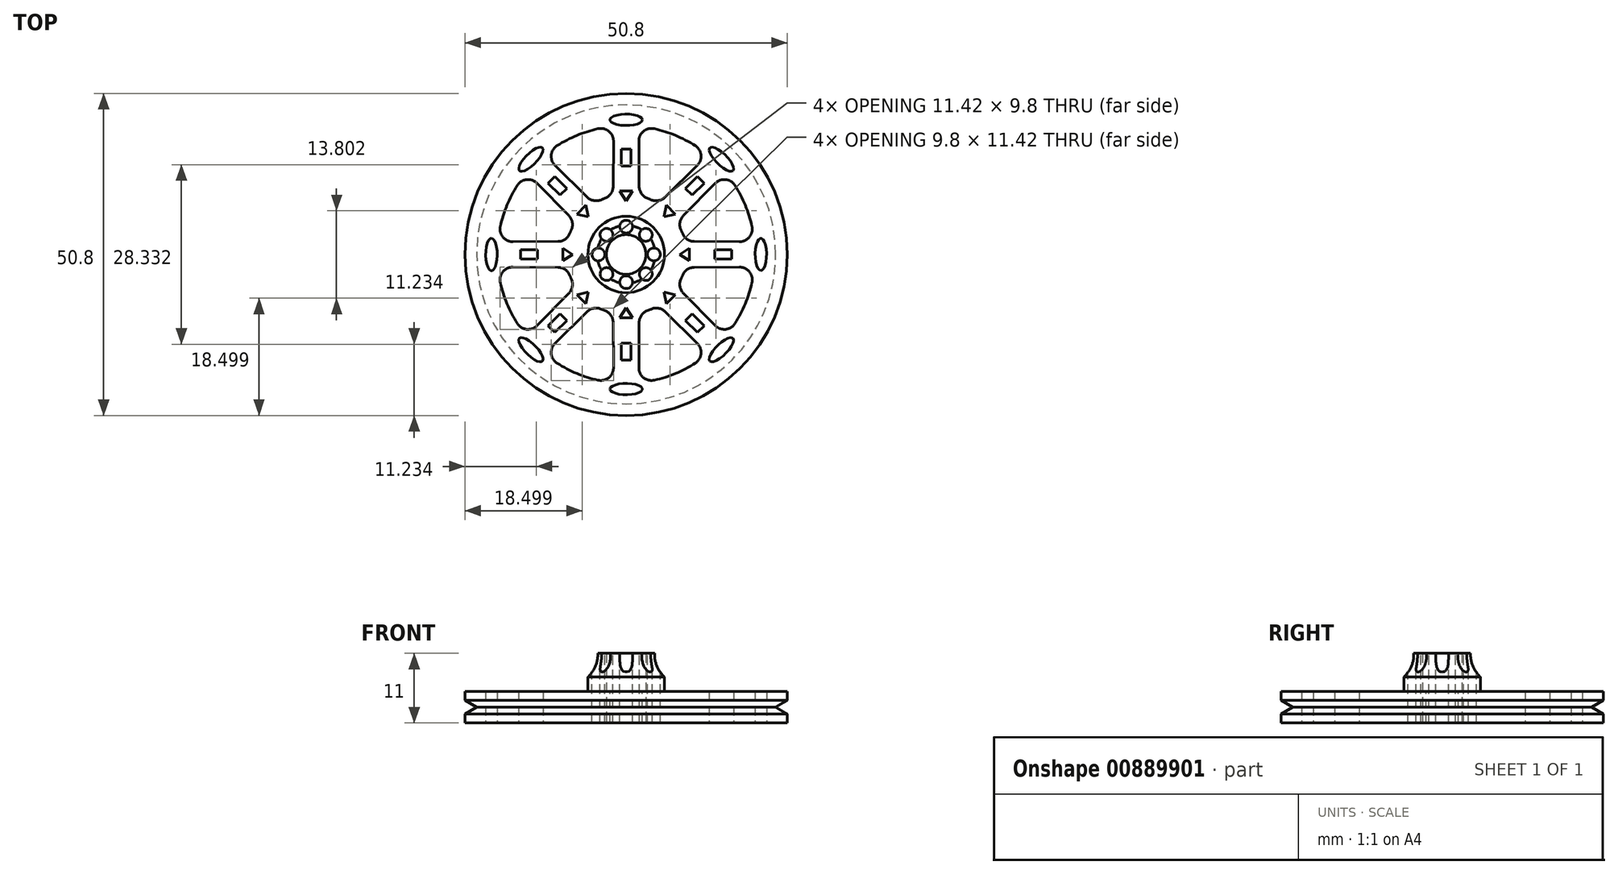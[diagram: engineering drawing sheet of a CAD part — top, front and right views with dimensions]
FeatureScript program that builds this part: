
annotation { "Feature Type Name" : "Feature", "Feature Type Description" : "" }
export const myFeature = defineFeature(function(context is Context, id is Id, definition is map)
    precondition{}
    {
        {
            var Q0;
            Q0=qCreatedBy(makeId("Top.planeOp"),FACE);
            var sketch = newSketch(context, id + "F0", { "sketchPlane" : qUnion([Q0])});
            skCircle(sketch, "E0", {"center": v(0, 0) * mm, "radius": 25.4 * mm});
            skCircle(sketch, "E1", {"center": v(0, 0) * mm, "radius": 3.12 * mm});
            skArc(sketch, "E2.0", {"start": v(-4.44, 19.83) * mm, "mid": v(-7.78, 18.77) * mm, "end": v(-10.88, 17.16) * mm});
            skArc(sketch, "E3.0", {"start": v(-3.34, 8.87) * mm, "mid": v(-3.63, 8.75) * mm, "end": v(-3.9, 8.63) * mm});
            skLineSegment(sketch, "E4.0", {"start": v(-2, 17.87) * mm, "end": v(-2.04, 10.73) * mm});
            skLineSegment(sketch, "E5.0", {"start": v(2, 17.87) * mm, "end": v(2.04, 10.73) * mm});
            skPoint(sketch, "E6.orphan", {"position": v(0, 22.85) * mm});
            skPoint(sketch, "E7.visualSharp", {"position": v(-1.99, 20.22) * mm});
            skArc(sketch, "E7.filletArc", {"start": v(-2, 17.87) * mm, "mid": v(-2.74, 19.44) * mm, "end": v(-4.44, 19.83) * mm});
            skPoint(sketch, "E8.visualSharp", {"position": v(1.99, 20.22) * mm});
            skArc(sketch, "E8.filletArc", {"start": v(4.44, 19.83) * mm, "mid": v(2.74, 19.44) * mm, "end": v(2, 17.87) * mm});
            skPoint(sketch, "E9.visualSharp", {"position": v(-2.05, 9.25) * mm});
            skArc(sketch, "E9.filletArc", {"start": v(-3.34, 8.87) * mm, "mid": v(-2.4, 9.6) * mm, "end": v(-2.04, 10.73) * mm});
            skPoint(sketch, "E10.visualSharp", {"position": v(2.05, 9.25) * mm});
            skArc(sketch, "E10.filletArc", {"start": v(2.04, 10.73) * mm, "mid": v(2.4, 9.6) * mm, "end": v(3.34, 8.87) * mm});
            skArc(sketch, "E11.1.0", {"start": v(-14.05, 11.22) * mm, "mid": v(-15.68, 11.8) * mm, "end": v(-17.16, 10.88) * mm});
            skLineSegment(sketch, "E11.1.1", {"start": v(-14.05, 11.22) * mm, "end": v(-9.03, 6.14) * mm});
            skArc(sketch, "E11.1.2", {"start": v(-8.63, 3.9) * mm, "mid": v(-8.48, 5.09) * mm, "end": v(-9.03, 6.14) * mm});
            skArc(sketch, "E11.1.3", {"start": v(-10.88, 17.16) * mm, "mid": v(-11.8, 15.68) * mm, "end": v(-11.22, 14.05) * mm});
            skLineSegment(sketch, "E11.1.4", {"start": v(-11.22, 14.05) * mm, "end": v(-6.14, 9.03) * mm});
            skArc(sketch, "E11.1.5", {"start": v(-6.14, 9.03) * mm, "mid": v(-5.09, 8.48) * mm, "end": v(-3.9, 8.63) * mm});
            skArc(sketch, "E11.2.0", {"start": v(-17.87, -2) * mm, "mid": v(-19.44, -2.74) * mm, "end": v(-19.83, -4.44) * mm});
            skLineSegment(sketch, "E11.2.1", {"start": v(-17.87, -2) * mm, "end": v(-10.73, -2.04) * mm});
            skArc(sketch, "E11.2.2", {"start": v(-8.87, -3.34) * mm, "mid": v(-9.6, -2.4) * mm, "end": v(-10.73, -2.04) * mm});
            skArc(sketch, "E11.2.3", {"start": v(-19.83, 4.44) * mm, "mid": v(-19.44, 2.74) * mm, "end": v(-17.87, 2) * mm});
            skLineSegment(sketch, "E11.2.4", {"start": v(-17.87, 2) * mm, "end": v(-10.73, 2.04) * mm});
            skArc(sketch, "E11.2.5", {"start": v(-10.73, 2.04) * mm, "mid": v(-9.6, 2.4) * mm, "end": v(-8.87, 3.34) * mm});
            skArc(sketch, "E11.3.0", {"start": v(-11.22, -14.05) * mm, "mid": v(-11.8, -15.68) * mm, "end": v(-10.88, -17.16) * mm});
            skLineSegment(sketch, "E11.3.1", {"start": v(-11.22, -14.05) * mm, "end": v(-6.14, -9.03) * mm});
            skArc(sketch, "E11.3.2", {"start": v(-3.9, -8.63) * mm, "mid": v(-5.09, -8.48) * mm, "end": v(-6.14, -9.03) * mm});
            skArc(sketch, "E11.3.3", {"start": v(-17.16, -10.88) * mm, "mid": v(-15.68, -11.8) * mm, "end": v(-14.05, -11.22) * mm});
            skLineSegment(sketch, "E11.3.4", {"start": v(-14.05, -11.22) * mm, "end": v(-9.03, -6.14) * mm});
            skArc(sketch, "E11.3.5", {"start": v(-9.03, -6.14) * mm, "mid": v(-8.48, -5.09) * mm, "end": v(-8.63, -3.9) * mm});
            skArc(sketch, "E11.4.0", {"start": v(2, -17.87) * mm, "mid": v(2.74, -19.44) * mm, "end": v(4.44, -19.83) * mm});
            skLineSegment(sketch, "E11.4.1", {"start": v(2, -17.87) * mm, "end": v(2.04, -10.73) * mm});
            skArc(sketch, "E11.4.2", {"start": v(3.34, -8.87) * mm, "mid": v(2.4, -9.6) * mm, "end": v(2.04, -10.73) * mm});
            skArc(sketch, "E11.4.3", {"start": v(-4.44, -19.83) * mm, "mid": v(-2.74, -19.44) * mm, "end": v(-2, -17.87) * mm});
            skLineSegment(sketch, "E11.4.4", {"start": v(-2, -17.87) * mm, "end": v(-2.04, -10.73) * mm});
            skArc(sketch, "E11.4.5", {"start": v(-2.04, -10.73) * mm, "mid": v(-2.4, -9.6) * mm, "end": v(-3.34, -8.87) * mm});
            skArc(sketch, "E11.5.0", {"start": v(14.05, -11.22) * mm, "mid": v(15.68, -11.8) * mm, "end": v(17.16, -10.88) * mm});
            skLineSegment(sketch, "E11.5.1", {"start": v(14.05, -11.22) * mm, "end": v(9.03, -6.14) * mm});
            skArc(sketch, "E11.5.2", {"start": v(8.63, -3.9) * mm, "mid": v(8.48, -5.09) * mm, "end": v(9.03, -6.14) * mm});
            skArc(sketch, "E11.5.3", {"start": v(10.88, -17.16) * mm, "mid": v(11.8, -15.68) * mm, "end": v(11.22, -14.05) * mm});
            skLineSegment(sketch, "E11.5.4", {"start": v(11.22, -14.05) * mm, "end": v(6.14, -9.03) * mm});
            skArc(sketch, "E11.5.5", {"start": v(6.14, -9.03) * mm, "mid": v(5.09, -8.48) * mm, "end": v(3.9, -8.63) * mm});
            skArc(sketch, "E11.6.0", {"start": v(17.87, 2) * mm, "mid": v(19.44, 2.74) * mm, "end": v(19.83, 4.44) * mm});
            skLineSegment(sketch, "E11.6.1", {"start": v(17.87, 2) * mm, "end": v(10.73, 2.04) * mm});
            skArc(sketch, "E11.6.2", {"start": v(8.87, 3.34) * mm, "mid": v(9.6, 2.4) * mm, "end": v(10.73, 2.04) * mm});
            skArc(sketch, "E11.6.3", {"start": v(19.83, -4.44) * mm, "mid": v(19.44, -2.74) * mm, "end": v(17.87, -2) * mm});
            skLineSegment(sketch, "E11.6.4", {"start": v(17.87, -2) * mm, "end": v(10.73, -2.04) * mm});
            skArc(sketch, "E11.6.5", {"start": v(10.73, -2.04) * mm, "mid": v(9.6, -2.4) * mm, "end": v(8.87, -3.34) * mm});
            skArc(sketch, "E11.7.0", {"start": v(11.22, 14.05) * mm, "mid": v(11.8, 15.68) * mm, "end": v(10.88, 17.16) * mm});
            skLineSegment(sketch, "E11.7.1", {"start": v(11.22, 14.05) * mm, "end": v(6.14, 9.03) * mm});
            skArc(sketch, "E11.7.2", {"start": v(3.9, 8.63) * mm, "mid": v(5.09, 8.48) * mm, "end": v(6.14, 9.03) * mm});
            skArc(sketch, "E11.7.3", {"start": v(17.16, 10.88) * mm, "mid": v(15.68, 11.8) * mm, "end": v(14.05, 11.22) * mm});
            skLineSegment(sketch, "E11.7.4", {"start": v(14.05, 11.22) * mm, "end": v(9.03, 6.14) * mm});
            skArc(sketch, "E11.7.5", {"start": v(9.03, 6.14) * mm, "mid": v(8.48, 5.09) * mm, "end": v(8.63, 3.9) * mm});
            skArc(sketch, "E12.trimOffspring", {"start": v(-17.16, 10.88) * mm, "mid": v(-18.77, 7.78) * mm, "end": v(-19.83, 4.44) * mm});
            skArc(sketch, "E13.trimOffspring", {"start": v(-8.63, 3.9) * mm, "mid": v(-8.75, 3.63) * mm, "end": v(-8.87, 3.34) * mm});
            skArc(sketch, "E14.trimOffspring", {"start": v(-8.87, -3.34) * mm, "mid": v(-8.75, -3.63) * mm, "end": v(-8.63, -3.9) * mm});
            skArc(sketch, "E15.trimOffspring", {"start": v(-19.83, -4.44) * mm, "mid": v(-18.77, -7.78) * mm, "end": v(-17.16, -10.88) * mm});
            skArc(sketch, "E16.trimOffspring", {"start": v(-10.88, -17.16) * mm, "mid": v(-7.78, -18.77) * mm, "end": v(-4.44, -19.83) * mm});
            skArc(sketch, "E17.trimOffspring", {"start": v(-3.9, -8.63) * mm, "mid": v(-3.63, -8.75) * mm, "end": v(-3.34, -8.87) * mm});
            skArc(sketch, "E18.trimOffspring", {"start": v(3.34, -8.87) * mm, "mid": v(3.63, -8.75) * mm, "end": v(3.9, -8.63) * mm});
            skArc(sketch, "E19.trimOffspring", {"start": v(8.63, -3.9) * mm, "mid": v(8.75, -3.63) * mm, "end": v(8.87, -3.34) * mm});
            skArc(sketch, "E20.trimOffspring", {"start": v(8.87, 3.34) * mm, "mid": v(8.75, 3.63) * mm, "end": v(8.63, 3.9) * mm});
            skArc(sketch, "E21.trimOffspring", {"start": v(3.9, 8.63) * mm, "mid": v(3.63, 8.75) * mm, "end": v(3.34, 8.87) * mm});
            skArc(sketch, "E22.trimOffspring", {"start": v(10.88, 17.16) * mm, "mid": v(7.78, 18.77) * mm, "end": v(4.44, 19.83) * mm});
            skArc(sketch, "E23.trimOffspring", {"start": v(19.83, 4.44) * mm, "mid": v(18.77, 7.78) * mm, "end": v(17.16, 10.88) * mm});
            skArc(sketch, "E24.trimOffspring", {"start": v(17.16, -10.88) * mm, "mid": v(18.77, -7.78) * mm, "end": v(19.83, -4.44) * mm});
            skArc(sketch, "E25.trimOffspring", {"start": v(4.44, -19.83) * mm, "mid": v(7.78, -18.77) * mm, "end": v(10.88, -17.16) * mm});
            skSolve(sketch);
        }
        {
            var Q0;
            Q0=makeQuery(id+"F0.imprint","IMPRINT",FACE,{"disambiguationData":[TD([[makeQuery(id+"F0.imprint","IMPRINT",EDGE,{"derivedFrom":sQuery(id+"F0.wireOp",EDGE,"E0")}),1.0]])]});
            extrude(context, id + "F1", {"entities" : qUnion([Q0]), "endBound" : BoundingType.SYMMETRIC, "depth" : 5 * mm, "offsetDistance" : 25.4 * mm});
        }
        {
            var Q0;
            Q0=makeQuery(id+"F1.opExtrude","CAP_FACE",FACE,{"disambiguationData":[OSD([sQuery(id+"F0.wireOp",EDGE,"E0"),sQuery(id+"F0.wireOp",EDGE,"E1"),sQuery(id+"F0.wireOp",EDGE,"E2.0"),sQuery(id+"F0.wireOp",EDGE,"E3.0"),sQuery(id+"F0.wireOp",EDGE,"E4.0"),sQuery(id+"F0.wireOp",EDGE,"E5.0"),sQuery(id+"F0.wireOp",EDGE,"E7.filletArc"),sQuery(id+"F0.wireOp",EDGE,"E8.filletArc"),sQuery(id+"F0.wireOp",EDGE,"E9.filletArc"),sQuery(id+"F0.wireOp",EDGE,"E10.filletArc"),sQuery(id+"F0.wireOp",EDGE,"E11.1.0"),sQuery(id+"F0.wireOp",EDGE,"E11.1.1"),sQuery(id+"F0.wireOp",EDGE,"E11.1.2"),sQuery(id+"F0.wireOp",EDGE,"E11.1.3"),sQuery(id+"F0.wireOp",EDGE,"E11.1.4"),sQuery(id+"F0.wireOp",EDGE,"E11.1.5"),sQuery(id+"F0.wireOp",EDGE,"E11.2.0"),sQuery(id+"F0.wireOp",EDGE,"E11.2.1"),sQuery(id+"F0.wireOp",EDGE,"E11.2.2"),sQuery(id+"F0.wireOp",EDGE,"E11.2.3"),sQuery(id+"F0.wireOp",EDGE,"E11.2.4"),sQuery(id+"F0.wireOp",EDGE,"E11.2.5"),sQuery(id+"F0.wireOp",EDGE,"E11.3.0"),sQuery(id+"F0.wireOp",EDGE,"E11.3.1"),sQuery(id+"F0.wireOp",EDGE,"E11.3.2"),sQuery(id+"F0.wireOp",EDGE,"E11.3.3"),sQuery(id+"F0.wireOp",EDGE,"E11.3.4"),sQuery(id+"F0.wireOp",EDGE,"E11.3.5"),sQuery(id+"F0.wireOp",EDGE,"E11.4.0"),sQuery(id+"F0.wireOp",EDGE,"E11.4.1"),sQuery(id+"F0.wireOp",EDGE,"E11.4.2"),sQuery(id+"F0.wireOp",EDGE,"E11.4.3"),sQuery(id+"F0.wireOp",EDGE,"E11.4.4"),sQuery(id+"F0.wireOp",EDGE,"E11.4.5"),sQuery(id+"F0.wireOp",EDGE,"E11.5.0"),sQuery(id+"F0.wireOp",EDGE,"E11.5.1"),sQuery(id+"F0.wireOp",EDGE,"E11.5.2"),sQuery(id+"F0.wireOp",EDGE,"E11.5.3"),sQuery(id+"F0.wireOp",EDGE,"E11.5.4"),sQuery(id+"F0.wireOp",EDGE,"E11.5.5"),sQuery(id+"F0.wireOp",EDGE,"E11.6.0"),sQuery(id+"F0.wireOp",EDGE,"E11.6.1"),sQuery(id+"F0.wireOp",EDGE,"E11.6.2"),sQuery(id+"F0.wireOp",EDGE,"E11.6.3"),sQuery(id+"F0.wireOp",EDGE,"E11.6.4"),sQuery(id+"F0.wireOp",EDGE,"E11.6.5"),sQuery(id+"F0.wireOp",EDGE,"E11.7.0"),sQuery(id+"F0.wireOp",EDGE,"E11.7.1"),sQuery(id+"F0.wireOp",EDGE,"E11.7.2"),sQuery(id+"F0.wireOp",EDGE,"E11.7.3"),sQuery(id+"F0.wireOp",EDGE,"E11.7.4"),sQuery(id+"F0.wireOp",EDGE,"E11.7.5"),sQuery(id+"F0.wireOp",EDGE,"E12.trimOffspring"),sQuery(id+"F0.wireOp",EDGE,"E13.trimOffspring"),sQuery(id+"F0.wireOp",EDGE,"E14.trimOffspring"),sQuery(id+"F0.wireOp",EDGE,"E15.trimOffspring"),sQuery(id+"F0.wireOp",EDGE,"E16.trimOffspring"),sQuery(id+"F0.wireOp",EDGE,"E17.trimOffspring"),sQuery(id+"F0.wireOp",EDGE,"E18.trimOffspring"),sQuery(id+"F0.wireOp",EDGE,"E19.trimOffspring"),sQuery(id+"F0.wireOp",EDGE,"E20.trimOffspring"),sQuery(id+"F0.wireOp",EDGE,"E21.trimOffspring"),sQuery(id+"F0.wireOp",EDGE,"E22.trimOffspring"),sQuery(id+"F0.wireOp",EDGE,"E23.trimOffspring"),sQuery(id+"F0.wireOp",EDGE,"E24.trimOffspring"),sQuery(id+"F0.wireOp",EDGE,"E25.trimOffspring")])],"isStart":false});
            var sketch = newSketch(context, id + "F2", { "sketchPlane" : qUnion([Q0])});
            skCircle(sketch, "E26", {"center": v(0, 0) * mm, "radius": 6.03 * mm});
            skSolve(sketch);
        }
        {
            var Q0;
            Q0=makeQuery(id+"F2.imprint","IMPRINT",FACE,{"disambiguationData":[TD([[makeQuery(id+"F2.imprint","IMPRINT",EDGE,{"derivedFrom":sQuery(id+"F2.wireOp",EDGE,"E26")}),1.0]])]});
            extrude(context, id + "F3", {"entities" : qUnion([Q0]), "operationType" : NewBodyOperationType.ADD, "depth" : 6 * mm, "offsetDistance" : 25.4 * mm});
        }
        {
            var Q0;
            Q0=makeQuery(id+"F3.opExtrude","CAP_FACE",FACE,{"disambiguationData":[OSD([sQuery(id+"F2.wireOp",EDGE,"E26")])],"isStart":false});
            var sketch = newSketch(context, id + "F4", { "sketchPlane" : qUnion([Q0])});
            skCircle(sketch, "E27", {"center": v(0, 0) * mm, "radius": 3 * mm});
            skSolve(sketch);
        }
        {
            var Q0;
            Q0=makeQuery(id+"F4.imprint","IMPRINT",FACE,{"disambiguationData":[TD([[makeQuery(id+"F4.imprint","IMPRINT",EDGE,{"derivedFrom":sQuery(id+"F4.wireOp",EDGE,"E27")}),1.0]])]});
            extrude(context, id + "F5", {"entities" : qUnion([Q0]), "operationType" : NewBodyOperationType.REMOVE, "endBound" : BoundingType.THROUGH_ALL, "oppositeDirection" : true, "depth" : 25.4 * mm, "offsetDistance" : 25.4 * mm});
        }
        {
            var Q0;
            Q0=qCreatedBy(makeId("Top.planeOp"),FACE);
            var sketch = newSketch(context, id + "F6", { "sketchPlane" : qUnion([Q0])});
            skCircle(sketch, "E28", {"center": v(0, 4.38) * mm, "radius": 1 * mm});
            skCircle(sketch, "E29.1.0", {"center": v(-3.1, 3.1) * mm, "radius": 1 * mm});
            skCircle(sketch, "E29.2.0", {"center": v(-4.38, 0) * mm, "radius": 1 * mm});
            skPoint(sketch, "E29.center", {"position": v(0, 0) * mm});
            skCircle(sketch, "E30.1.3.0", {"center": v(-3.1, -3.1) * mm, "radius": 1 * mm});
            skCircle(sketch, "E30.1.4.0", {"center": v(0, -4.38) * mm, "radius": 1 * mm});
            skCircle(sketch, "E30.1.5.0", {"center": v(3.1, -3.1) * mm, "radius": 1 * mm});
            skCircle(sketch, "E30.1.6.0", {"center": v(4.38, 0) * mm, "radius": 1 * mm});
            skCircle(sketch, "E30.1.7.0", {"center": v(3.1, 3.1) * mm, "radius": 1 * mm});
            skSolve(sketch);
        }
        {
            var Q0;
            Q0=qSketchRegion(id+"F6",true);
            extrude(context, id + "F7", {"entities" : qUnion([Q0]), "operationType" : NewBodyOperationType.REMOVE, "endBound" : BoundingType.SYMMETRIC, "oppositeDirection" : true, "depth" : 25.4 * mm, "offsetDistance" : 25.4 * mm});
        }
        {
            var Q0;
            Q0=qCreatedBy(makeId("Front.planeOp"),FACE);
            var sketch = newSketch(context, id + "F8", { "sketchPlane" : qUnion([Q0])});
            skLineSegment(sketch, "E31", {"start": v(0, 0) * mm, "end": v(0, 31.12) * mm, "construction": true});
            skCircle(sketch, "E32", {"center": v(-9.67, 8.29) * mm, "radius": 5.08 * mm});
            skSolve(sketch);
        }
        {
            var Q0;
            Q0 = qSketchRegion(id + "F8", true);
            var Q1;
            Q1=sQuery(id+"F8.wireOp",EDGE,"E31");
            revolve(context, id + "F9", {"operationType" : NewBodyOperationType.REMOVE, "surfaceOperationType" : NewSurfaceOperationType.NEW, "entities" : qUnion([Q0]), "axis" : qUnion([Q1]), "revolveType" : RevolveType.FULL, "oppositeDirection" : true});
        }
        {
            var Q0;
            Q0=qCreatedBy(makeId("Front.planeOp"),FACE);
            var sketch = newSketch(context, id + "F10", { "sketchPlane" : qUnion([Q0])});
            skLineSegment(sketch, "E33", {"start": v(-25.57, 0) * mm, "end": v(-23.57, 0) * mm});
            skLineSegment(sketch, "E34", {"start": v(-23.57, 0) * mm, "end": v(-25.4, -1.07) * mm});
            skLineSegment(sketch, "E35", {"start": v(-25.4, -1.08) * mm, "end": v(-25.57, 0) * mm});
            skLineSegment(sketch, "E36.MirrorCS", {"start": v(-23.57, 0) * mm, "end": v(-25.4, 1.08) * mm});
            skLineSegment(sketch, "E37.MirrorCS", {"start": v(-25.4, 1.08) * mm, "end": v(-25.57, 0) * mm});
            skLineSegment(sketch, "E38", {"start": v(0, 0) * mm, "end": v(0, 11.24) * mm, "construction": true});
            skSolve(sketch);
        }
        {
            var Q0;
            Q0 = qSketchRegion(id + "F10", true);
            var Q1;
            Q1=sQuery(id+"F10.wireOp",EDGE,"E38");
            revolve(context, id + "F11", {"operationType" : NewBodyOperationType.REMOVE, "surfaceOperationType" : NewSurfaceOperationType.NEW, "entities" : qUnion([Q0]), "axis" : qUnion([Q1]), "revolveType" : RevolveType.FULL, "oppositeDirection" : true});
        }
        {
            var Q0;
            Q0=qCreatedBy(makeId("Top.planeOp"),FACE);
            var sketch = newSketch(context, id + "F12", { "sketchPlane" : qUnion([Q0])});
            skEllipse(sketch, "E39", {"center": v(0, 21.24) * mm, "majorRadius": 2.56 * mm, "minorRadius": 0.9 * mm, "majorAxis": v(1, 0)});
            skEllipse(sketch, "E40.1.0", {"center": v(-15.02, 15.02) * mm, "majorRadius": 2.56 * mm, "minorRadius": 0.9 * mm, "majorAxis": v(0.7, 0.7)});
            skEllipse(sketch, "E40.2.0", {"center": v(-21.24, 0) * mm, "majorRadius": 2.56 * mm, "minorRadius": 0.9 * mm, "majorAxis": v(0, 1)});
            skPoint(sketch, "E40.center", {"position": v(0, 0) * mm});
            skEllipse(sketch, "E41.1.3.0", {"center": v(-15.02, -15.02) * mm, "majorRadius": 2.56 * mm, "minorRadius": 0.9 * mm, "majorAxis": v(-0.7, 0.7)});
            skEllipse(sketch, "E41.1.4.0", {"center": v(0, -21.24) * mm, "majorRadius": 2.56 * mm, "minorRadius": 0.9 * mm, "majorAxis": v(-1, 0)});
            skEllipse(sketch, "E41.1.5.0", {"center": v(15.02, -15.02) * mm, "majorRadius": 2.56 * mm, "minorRadius": 0.9 * mm, "majorAxis": v(-0.7, -0.7)});
            skEllipse(sketch, "E41.1.6.0", {"center": v(21.24, 0) * mm, "majorRadius": 2.56 * mm, "minorRadius": 0.9 * mm, "majorAxis": v(0, -1)});
            skEllipse(sketch, "E41.1.7.0", {"center": v(15.02, 15.02) * mm, "majorRadius": 2.56 * mm, "minorRadius": 0.9 * mm, "majorAxis": v(0.7, -0.7)});
            skSolve(sketch);
        }
        {
            var Q0;
            Q0 = qSketchRegion(id + "F12", true);
            extrude(context, id + "F13", {"entities" : qUnion([Q0]), "operationType" : NewBodyOperationType.REMOVE, "endBound" : BoundingType.SYMMETRIC, "oppositeDirection" : true, "depth" : 25.4 * mm, "offsetDistance" : 25.4 * mm});
        }
        {
            var Q0;
            Q0=qCreatedBy(makeId("Top.planeOp"),FACE);
            var sketch = newSketch(context, id + "F14", { "sketchPlane" : qUnion([Q0])});
            skLineSegment(sketch, "E42", {"start": v(0, 10) * mm, "end": v(0, 8.43) * mm});
            skLineSegment(sketch, "E43", {"start": v(0, 8.43) * mm, "end": v(-1, 10) * mm});
            skLineSegment(sketch, "E44", {"start": v(-1, 10) * mm, "end": v(0, 10) * mm});
            skLineSegment(sketch, "E45.MirrorCS", {"start": v(0, 8.43) * mm, "end": v(1, 10) * mm});
            skLineSegment(sketch, "E46.MirrorCS", {"start": v(1, 10) * mm, "end": v(0, 10) * mm});
            skLineSegment(sketch, "E47.1.0", {"start": v(-7.77, 6.36) * mm, "end": v(-7.07, 7.07) * mm});
            skLineSegment(sketch, "E47.1.1", {"start": v(-6.36, 7.77) * mm, "end": v(-7.07, 7.07) * mm});
            skLineSegment(sketch, "E47.1.2", {"start": v(-5.96, 5.96) * mm, "end": v(-6.36, 7.77) * mm});
            skLineSegment(sketch, "E47.1.3", {"start": v(-5.96, 5.96) * mm, "end": v(-7.77, 6.36) * mm});
            skLineSegment(sketch, "E47.2.0", {"start": v(-10, -1) * mm, "end": v(-10, 0) * mm});
            skLineSegment(sketch, "E47.2.1", {"start": v(-10, 1) * mm, "end": v(-10, 0) * mm});
            skLineSegment(sketch, "E47.2.2", {"start": v(-8.43, 0) * mm, "end": v(-10, 1) * mm});
            skLineSegment(sketch, "E47.2.3", {"start": v(-8.43, 0) * mm, "end": v(-10, -1) * mm});
            skPoint(sketch, "E47.center", {"position": v(0, 0) * mm});
            skLineSegment(sketch, "E48.1.3.0", {"start": v(-6.36, -7.77) * mm, "end": v(-7.07, -7.07) * mm});
            skLineSegment(sketch, "E48.3.3.0", {"start": v(-7.77, -6.36) * mm, "end": v(-7.07, -7.07) * mm});
            skLineSegment(sketch, "E48.6.3.0", {"start": v(-5.96, -5.96) * mm, "end": v(-7.77, -6.36) * mm});
            skLineSegment(sketch, "E48.9.3.0", {"start": v(-5.96, -5.96) * mm, "end": v(-6.36, -7.77) * mm});
            skLineSegment(sketch, "E48.1.4.0", {"start": v(1, -10) * mm, "end": v(0, -10) * mm});
            skLineSegment(sketch, "E48.3.4.0", {"start": v(-1, -10) * mm, "end": v(0, -10) * mm});
            skLineSegment(sketch, "E48.6.4.0", {"start": v(0, -8.43) * mm, "end": v(-1, -10) * mm});
            skLineSegment(sketch, "E48.9.4.0", {"start": v(0, -8.43) * mm, "end": v(1, -10) * mm});
            skLineSegment(sketch, "E48.1.5.0", {"start": v(7.77, -6.36) * mm, "end": v(7.07, -7.07) * mm});
            skLineSegment(sketch, "E48.3.5.0", {"start": v(6.36, -7.77) * mm, "end": v(7.07, -7.07) * mm});
            skLineSegment(sketch, "E48.6.5.0", {"start": v(5.96, -5.96) * mm, "end": v(6.36, -7.77) * mm});
            skLineSegment(sketch, "E48.9.5.0", {"start": v(5.96, -5.96) * mm, "end": v(7.77, -6.36) * mm});
            skLineSegment(sketch, "E48.1.6.0", {"start": v(10, 1) * mm, "end": v(10, 0) * mm});
            skLineSegment(sketch, "E48.3.6.0", {"start": v(10, -1) * mm, "end": v(10, 0) * mm});
            skLineSegment(sketch, "E48.6.6.0", {"start": v(8.43, 0) * mm, "end": v(10, -1) * mm});
            skLineSegment(sketch, "E48.9.6.0", {"start": v(8.43, 0) * mm, "end": v(10, 1) * mm});
            skLineSegment(sketch, "E48.1.7.0", {"start": v(6.36, 7.77) * mm, "end": v(7.07, 7.07) * mm});
            skLineSegment(sketch, "E48.3.7.0", {"start": v(7.77, 6.36) * mm, "end": v(7.07, 7.07) * mm});
            skLineSegment(sketch, "E48.6.7.0", {"start": v(5.96, 5.96) * mm, "end": v(7.77, 6.36) * mm});
            skLineSegment(sketch, "E48.9.7.0", {"start": v(5.96, 5.96) * mm, "end": v(6.36, 7.77) * mm});
            skSolve(sketch);
        }
        {
            var Q0;
            Q0 = qSketchRegion(id + "F14", true);
            extrude(context, id + "F15", {"entities" : qUnion([Q0]), "operationType" : NewBodyOperationType.REMOVE, "endBound" : BoundingType.SYMMETRIC, "oppositeDirection" : true, "depth" : 25.4 * mm, "offsetDistance" : 25.4 * mm});
        }
        {
            var Q0;
            Q0=qCreatedBy(makeId("Top.planeOp"),FACE);
            var sketch = newSketch(context, id + "F16", { "sketchPlane" : qUnion([Q0])});
            skLineSegment(sketch, "E49.bottom", {"start": v(0.75, 16.64) * mm, "end": v(-0.75, 16.64) * mm});
            skLineSegment(sketch, "E49.top", {"start": v(0.75, 13.97) * mm, "end": v(-0.75, 13.97) * mm});
            skLineSegment(sketch, "E49.left", {"start": v(0.75, 16.64) * mm, "end": v(0.75, 13.97) * mm});
            skLineSegment(sketch, "E49.right", {"start": v(-0.75, 16.64) * mm, "end": v(-0.75, 13.97) * mm});
            skPoint(sketch, "E49.middle", {"position": v(0, 15.3) * mm});
            skLineSegment(sketch, "E50.1.0", {"start": v(-12.3, 11.24) * mm, "end": v(-10.4, 9.35) * mm});
            skLineSegment(sketch, "E50.1.1", {"start": v(-11.24, 12.3) * mm, "end": v(-12.3, 11.24) * mm});
            skLineSegment(sketch, "E50.1.2", {"start": v(-11.24, 12.3) * mm, "end": v(-9.35, 10.4) * mm});
            skLineSegment(sketch, "E50.1.3", {"start": v(-9.35, 10.4) * mm, "end": v(-10.4, 9.35) * mm});
            skLineSegment(sketch, "E50.2.0", {"start": v(-16.64, -0.75) * mm, "end": v(-13.97, -0.75) * mm});
            skLineSegment(sketch, "E50.2.1", {"start": v(-16.64, 0.75) * mm, "end": v(-16.64, -0.75) * mm});
            skLineSegment(sketch, "E50.2.2", {"start": v(-16.64, 0.75) * mm, "end": v(-13.97, 0.75) * mm});
            skLineSegment(sketch, "E50.2.3", {"start": v(-13.97, 0.75) * mm, "end": v(-13.97, -0.75) * mm});
            skPoint(sketch, "E50.center", {"position": v(0, 0) * mm});
            skLineSegment(sketch, "E51.3.3.0", {"start": v(-12.3, -11.24) * mm, "end": v(-11.24, -12.3) * mm});
            skLineSegment(sketch, "E51.6.3.0", {"start": v(-12.3, -11.24) * mm, "end": v(-10.4, -9.35) * mm});
            skLineSegment(sketch, "E51.8.3.0", {"start": v(-11.24, -12.3) * mm, "end": v(-9.35, -10.4) * mm});
            skLineSegment(sketch, "E51.9.3.0", {"start": v(-10.4, -9.35) * mm, "end": v(-9.35, -10.4) * mm});
            skLineSegment(sketch, "E51.3.4.0", {"start": v(-0.75, -16.64) * mm, "end": v(0.75, -16.64) * mm});
            skLineSegment(sketch, "E51.6.4.0", {"start": v(-0.75, -16.64) * mm, "end": v(-0.75, -13.97) * mm});
            skLineSegment(sketch, "E51.8.4.0", {"start": v(0.75, -16.64) * mm, "end": v(0.75, -13.97) * mm});
            skLineSegment(sketch, "E51.9.4.0", {"start": v(-0.75, -13.97) * mm, "end": v(0.75, -13.97) * mm});
            skLineSegment(sketch, "E51.3.5.0", {"start": v(11.24, -12.3) * mm, "end": v(12.3, -11.24) * mm});
            skLineSegment(sketch, "E51.6.5.0", {"start": v(11.24, -12.3) * mm, "end": v(9.35, -10.4) * mm});
            skLineSegment(sketch, "E51.8.5.0", {"start": v(12.3, -11.24) * mm, "end": v(10.4, -9.35) * mm});
            skLineSegment(sketch, "E51.9.5.0", {"start": v(9.35, -10.4) * mm, "end": v(10.4, -9.35) * mm});
            skLineSegment(sketch, "E51.3.6.0", {"start": v(16.64, -0.75) * mm, "end": v(16.64, 0.75) * mm});
            skLineSegment(sketch, "E51.6.6.0", {"start": v(16.64, -0.75) * mm, "end": v(13.97, -0.75) * mm});
            skLineSegment(sketch, "E51.8.6.0", {"start": v(16.64, 0.75) * mm, "end": v(13.97, 0.75) * mm});
            skLineSegment(sketch, "E51.9.6.0", {"start": v(13.97, -0.75) * mm, "end": v(13.97, 0.75) * mm});
            skLineSegment(sketch, "E51.3.7.0", {"start": v(12.3, 11.24) * mm, "end": v(11.24, 12.3) * mm});
            skLineSegment(sketch, "E51.6.7.0", {"start": v(12.3, 11.24) * mm, "end": v(10.4, 9.35) * mm});
            skLineSegment(sketch, "E51.8.7.0", {"start": v(11.24, 12.3) * mm, "end": v(9.35, 10.4) * mm});
            skLineSegment(sketch, "E51.9.7.0", {"start": v(10.4, 9.35) * mm, "end": v(9.35, 10.4) * mm});
            skSolve(sketch);
        }
        {
            var Q0;
            Q0 = qSketchRegion(id + "F16", true);
            extrude(context, id + "F17", {"entities" : qUnion([Q0]), "operationType" : NewBodyOperationType.REMOVE, "endBound" : BoundingType.SYMMETRIC, "oppositeDirection" : true, "depth" : 25.4 * mm, "offsetDistance" : 25.4 * mm});
        }
    });
